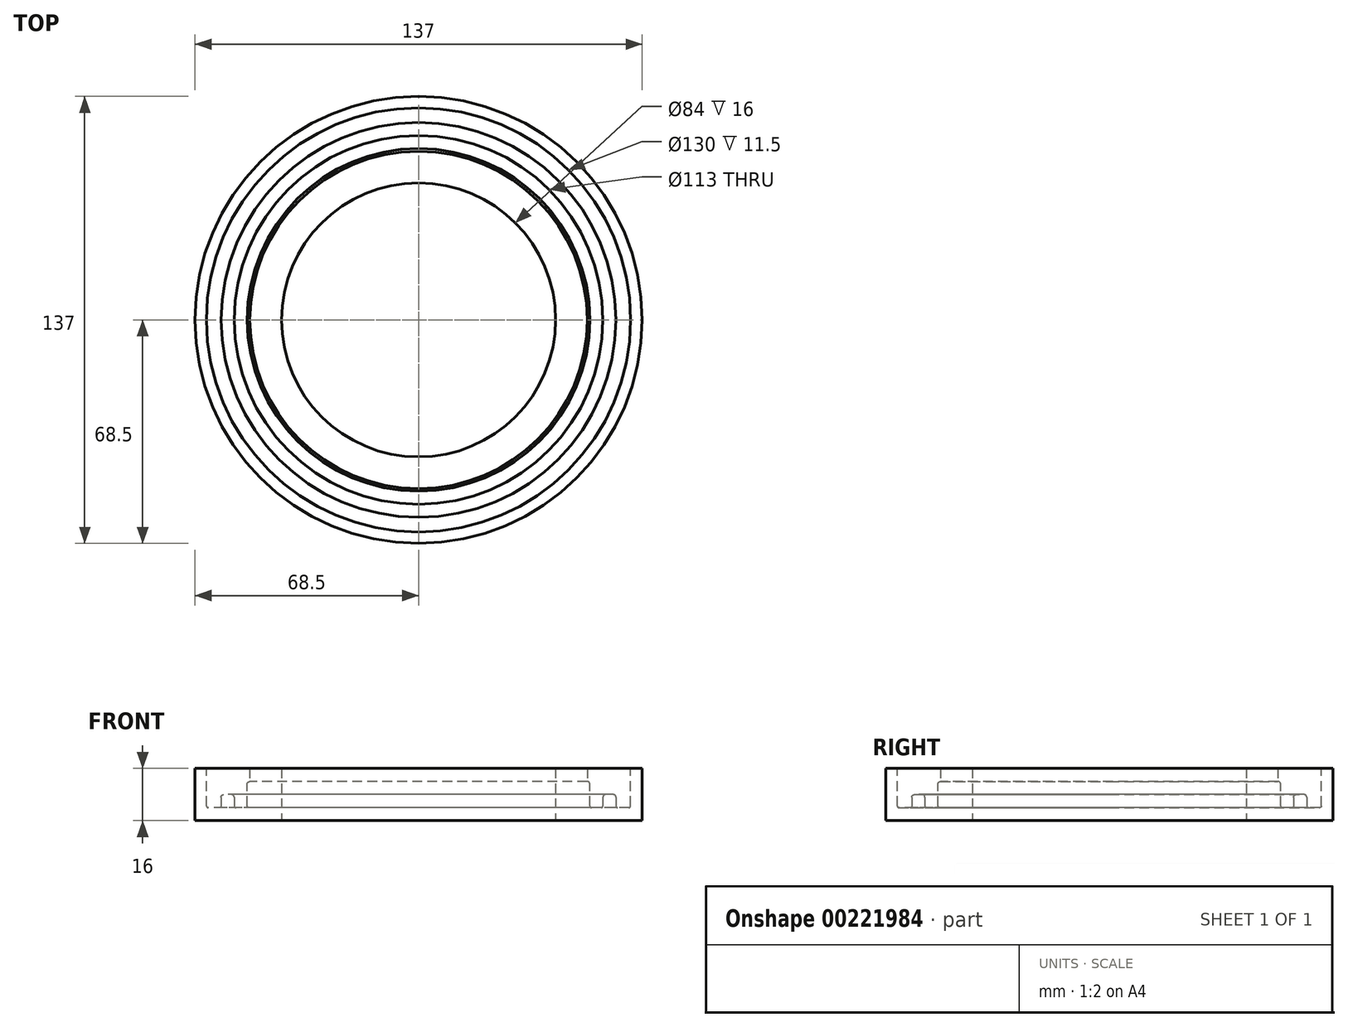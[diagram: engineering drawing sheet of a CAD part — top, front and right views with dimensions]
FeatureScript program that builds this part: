
annotation { "Feature Type Name" : "Feature", "Feature Type Description" : "" }
export const myFeature = defineFeature(function(context is Context, id is Id, definition is map)
    precondition{}
    {
        {
            var Q0;
            Q0=qCreatedBy(makeId("Top.planeOp"),FACE);
            var sketch = newSketch(context, id + "F0", { "sketchPlane" : qUnion([Q0])});
            skCircle(sketch, "E0", {"center": v(0, 0) * mm, "radius": 68.5 * mm});
            skCircle(sketch, "E1", {"center": v(0, 0) * mm, "radius": 42 * mm});
            skSolve(sketch);
        }
        {
            var Q0;
            Q0 = qSketchRegion(id + "F0", true);
            extrude(context, id + "F1", {"entities" : qUnion([Q0]), "depth" : 12 * mm});
        }
        {
            var Q0;
            Q0=makeQuery(id+"F1.opExtrude","CAP_FACE",FACE,{"disambiguationData":[OSD([sQuery(id+"F0.wireOp",EDGE,"E0"),sQuery(id+"F0.wireOp",EDGE,"E1")])],"isStart":false});
            cPlane(context, id + "F2", {"entities" : qUnion([Q0]), "cplaneType" : CPlaneType.OFFSET, "offset" : 0 * mm, "width" : 150 * mm, "height" : 150 * mm});
        }
        {
            var Q0;
            Q0=qCreatedBy(id+"F2.planeOp",FACE);
            var sketch = newSketch(context, id + "F3", { "sketchPlane" : qUnion([Q0])});
            skCircle(sketch, "E2", {"center": v(0, 0) * mm, "radius": 65 * mm});
            skCircle(sketch, "E3", {"center": v(0, 0) * mm, "radius": 52.5 * mm});
            skSolve(sketch);
        }
        {
            var Q0;
            Q0=makeQuery(id+"F3.imprint","IMPRINT",FACE,{"disambiguationData":[TD([[makeQuery(id+"F3.imprint","IMPRINT",EDGE,{"derivedFrom":sQuery(id+"F3.wireOp",EDGE,"E2")}),1.0]])]});
            extrude(context, id + "F4", {"entities" : qUnion([Q0]), "operationType" : NewBodyOperationType.REMOVE, "oppositeDirection" : true, "depth" : 8 * mm});
        }
        {
            var Q0;
            Q0=makeQuery(id+"F4.boolean.opBoolean","COPY",FACE,{"derivedFrom":makeQuery(id+"F4.opExtrude","CAP_FACE",FACE,{"disambiguationData":[OSD([sQuery(id+"F3.wireOp",EDGE,"E2"),sQuery(id+"F3.wireOp",EDGE,"E3")])],"isStart":false})});
            cPlane(context, id + "F5", {"entities" : qUnion([Q0]), "cplaneType" : CPlaneType.OFFSET, "offset" : 0 * mm, "width" : 150 * mm, "height" : 150 * mm});
        }
        {
            var Q0;
            Q0=qCreatedBy(id+"F5.planeOp",FACE);
            var sketch = newSketch(context, id + "F6", { "sketchPlane" : qUnion([Q0])});
            skCircle(sketch, "E4", {"center": v(0, 0) * mm, "radius": 60.5 * mm});
            skCircle(sketch, "E5", {"center": v(0, 0) * mm, "radius": 56.5 * mm});
            skSolve(sketch);
        }
        {
            var Q0;
            Q0=makeQuery(id+"F6.imprint","IMPRINT",FACE,{"disambiguationData":[TD([[makeQuery(id+"F6.imprint","IMPRINT",EDGE,{"derivedFrom":sQuery(id+"F6.wireOp",EDGE,"E4")}),1.0]])]});
            extrude(context, id + "F7", {"entities" : qUnion([Q0]), "operationType" : NewBodyOperationType.ADD, "depth" : 4 * mm});
        }
        {
            var Q0;
            Q0=makeQuery(id+"F7.opExtrude","CAP_EDGE",EDGE,{"disambiguationData":[OSD([sQuery(id+"F6.wireOp",EDGE,"E4")])],"isStart":false});
            var Q1;
            Q1=makeQuery(id+"F7.opExtrude","CAP_EDGE",EDGE,{"disambiguationData":[OSD([sQuery(id+"F6.wireOp",EDGE,"E5")])],"isStart":false});
            var Q2;
            Q2=makeQuery(id+"F4.boolean.opBoolean","COPY",EDGE,{"derivedFrom":makeQuery(id+"F4.opExtrude","CAP_EDGE",EDGE,{"disambiguationData":[OSD([sQuery(id+"F3.wireOp",EDGE,"E2")])],"isStart":true})});
            var Q3;
            Q3=makeQuery(id+"F4.boolean.opBoolean","COPY",EDGE,{"derivedFrom":makeQuery(id+"F4.opExtrude","CAP_EDGE",EDGE,{"disambiguationData":[OSD([sQuery(id+"F3.wireOp",EDGE,"E3")])],"isStart":true})});
            fillet(context, id + "F8", {"entities" : qUnion([Q0, Q1, Q2, Q3]), "radius" : .8 * mm, "tangentPropagation" : true, "allowEdgeOverflow" : false});
        }
        {
            var Q0;
            {var subQ0=sQuery(id+"F3.wireOp",EDGE,"E2");Q0=makeQuery(id+"F7.boolean.opBoolean","SPLIT",FACE,{"disambiguationData":[TD([makeQuery(id+"F4.boolean.opBoolean","COPY",FACE,{"derivedFrom":makeQuery(id+"F4.opExtrude","SWEPT_FACE",FACE,{"disambiguationData":[OSD([subQ0])]})})])],"derivedFrom":makeQuery(id+"F4.boolean.opBoolean","COPY",FACE,{"derivedFrom":makeQuery(id+"F4.opExtrude","CAP_FACE",FACE,{"disambiguationData":[OSD([subQ0,sQuery(id+"F3.wireOp",EDGE,"E3")])],"isStart":false})})});}
            var Q1;
            Q1=makeQuery(id+"F7.opExtrude","CAP_EDGE",EDGE,{"disambiguationData":[OSD([sQuery(id+"F6.wireOp",EDGE,"E5")])],"isStart":true});
            var Q2;
            Q2=makeQuery(id+"F4.boolean.opBoolean","COPY",EDGE,{"derivedFrom":makeQuery(id+"F4.opExtrude","CAP_EDGE",EDGE,{"disambiguationData":[OSD([sQuery(id+"F3.wireOp",EDGE,"E3")])],"isStart":false})});
            fillet(context, id + "F9", {"entities" : qUnion([Q0, Q1, Q2]), "radius" : .5 * mm, "tangentPropagation" : true, "allowEdgeOverflow" : false});
        }
        {
            var Q0;
            {var subQ0=sQuery(id+"F0.wireOp",EDGE,"E0");Q0=makeQuery(id+"F4.boolean.opBoolean","SPLIT",FACE,{"disambiguationData":[TD([makeQuery(id+"F1.opExtrude","SWEPT_FACE",FACE,{"disambiguationData":[OSD([subQ0])]})])],"derivedFrom":makeQuery(id+"F1.opExtrude","CAP_FACE",FACE,{"disambiguationData":[OSD([subQ0,sQuery(id+"F0.wireOp",EDGE,"E1")])],"isStart":false})});}
            var Q1;
            {var subQ0=sQuery(id+"F0.wireOp",EDGE,"E1");Q1=makeQuery(id+"F4.boolean.opBoolean","SPLIT",FACE,{"disambiguationData":[TD([makeQuery(id+"F1.opExtrude","SWEPT_FACE",FACE,{"disambiguationData":[OSD([subQ0])]})])],"derivedFrom":makeQuery(id+"F1.opExtrude","CAP_FACE",FACE,{"disambiguationData":[OSD([sQuery(id+"F0.wireOp",EDGE,"E0"),subQ0])],"isStart":false})});}
            extrude(context, id + "F10", {"entities" : qUnion([Q0, Q1]), "operationType" : NewBodyOperationType.ADD, "depth" : 4 * mm});
        }
    });
